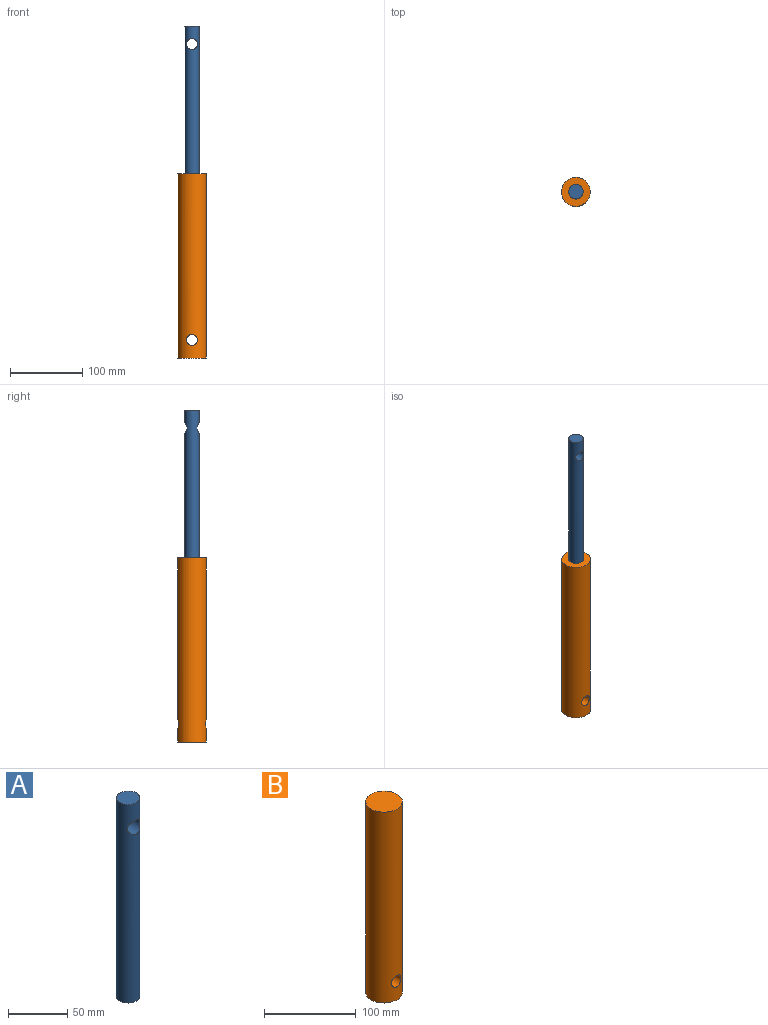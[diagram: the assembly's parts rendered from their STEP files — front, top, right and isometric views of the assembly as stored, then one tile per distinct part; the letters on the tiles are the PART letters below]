
ASSEMBLY  parts=2 mates=1
PART A: 4 faces, bbox 20x20x205 mm
  f0: cylinder r=10mm len=205mm, axis (0,0,1), area 12494.3mm2, adj f1,f2,f3
  f1: plane 20x20mm, normal (0,0,-1), area 314.2mm2, adj f0
  f2: plane 20x20mm, normal (0,0,1), area 314.2mm2, adj f0
  f3: cylinder r=7.5mm len=20mm, axis (0,-1,0), area 791mm2, adj f0
PART B: 4 faces, bbox 40x40x255 mm
  f0: cylinder r=20mm len=255mm, axis (0,0,-1), area 31684.9mm2, adj f1,f2,f3
  f1: plane 40x40mm, normal (0,0,1), area 1256.6mm2, adj f0
  f2: plane 40x40mm, normal (0,0,-1), area 1256.6mm2, adj f0
  f3: cylinder r=7.5mm len=40mm, axis (0,-1,0), area 1816.8mm2, adj f0
PLACE A t=(-75.07,-50.23,399.4)mm
PLACE B t=(-75.07,-50.23,-10.6)mm
MATE slider A.f0 <-> B.f0  axis (0,0,-1) through (-75.07,-50.23,219.4)mm
